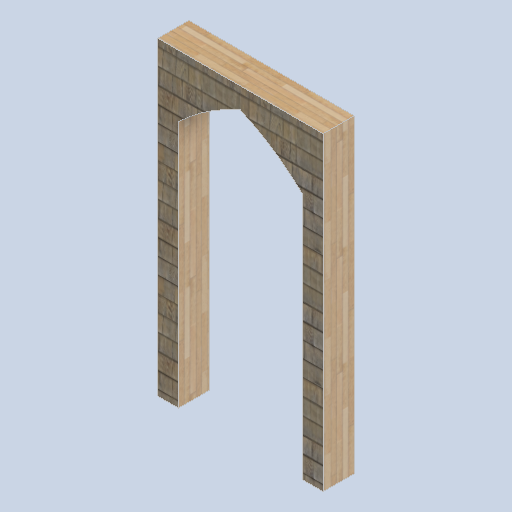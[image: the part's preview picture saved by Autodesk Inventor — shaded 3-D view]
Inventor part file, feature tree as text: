
AUTODESK INVENTOR PART (.ipt)
format: ipt  version: 2024.2 (Build 282272000, 272)  size: 378,368 bytes
history: native  units: mm
features: extrude x2, sketch x2
ambient origin geometry x8: Origin, YZ Plane, XZ Plane, XY Plane, X Axis, Y Axis, Z Axis, Center Point
bodies: Solid1 (feature_tree)
feature tree (4):
  extrude  "Extrusion1"  Depth=2000.0mm
  extrude  "Extrusion2"  TaperAngle=0.0deg  [1 undecoded]
  sketch  "Sketch1"  dims[d0=300.0mm d1=0.0mm d8=2000.0mm]
  sketch  "Sketch2"  dims[d9=2000.0mm d10=0.0mm d11=0.0mm d6=500.0mm d7=0.872665mm]
note: 1 required parameter value undecoded (feature->parameter linkage not recoverable at this tier; creation-order binding heuristic only, values carry confidence <= 0.55)
